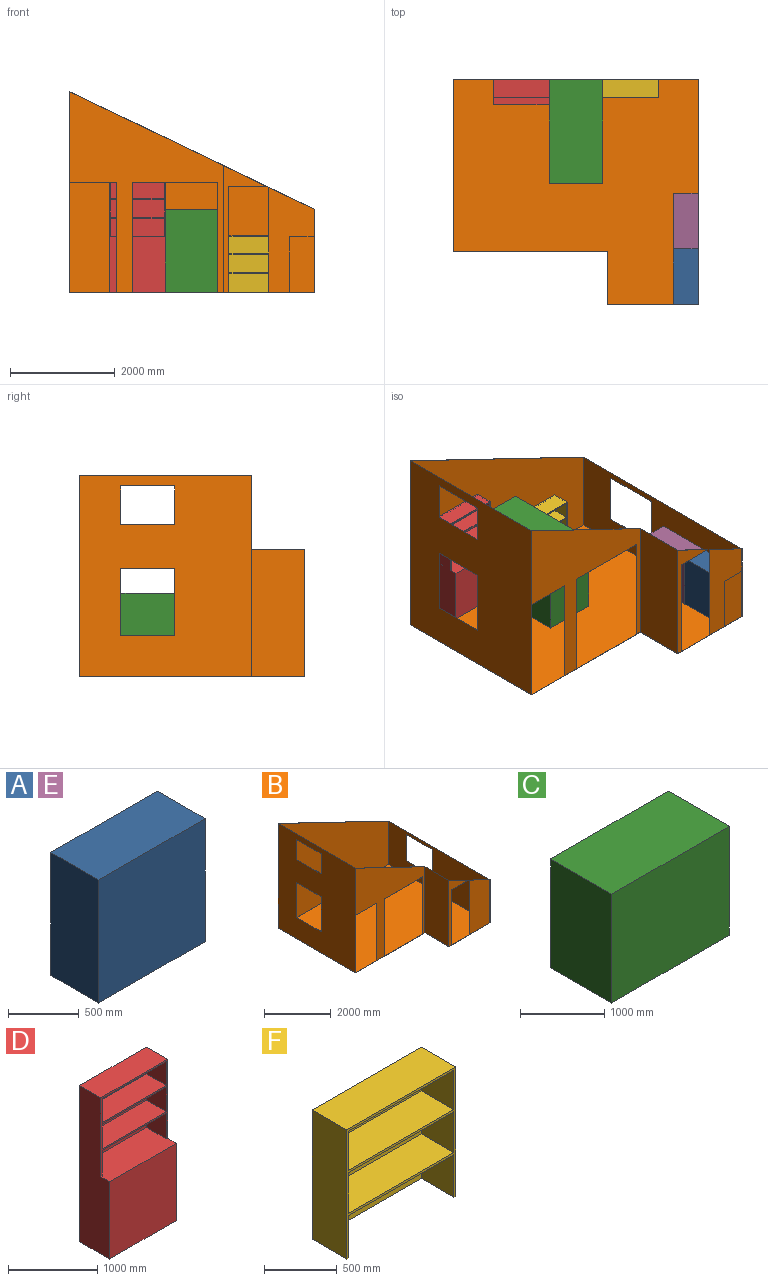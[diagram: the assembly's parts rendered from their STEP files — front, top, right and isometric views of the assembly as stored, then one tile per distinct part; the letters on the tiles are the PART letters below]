
ASSEMBLY  parts=6 mates=5
PART A: 6 faces, bbox 1060.5x476.3x1060.5 mm
  f0: plane 1060.45x1060.45mm, normal (0,1,0), area 1124554.2mm2, adj f2,f3,f4,f5
  f1: plane 1060.45x1060.45mm, normal (0,-1,0), area 1124554.2mm2, adj f2,f3,f4,f5
  f2: plane 1060.45x476.25mm, normal (1,0,0), area 505039.3mm2, adj f0,f1,f4,f5
  f3: plane 1060.45x476.25mm, normal (-1,0,0), area 505039.3mm2, adj f0,f1,f4,f5
  f4: plane 1060.45x476.25mm, normal (0,0,-1), area 505039.3mm2, adj f0,f1,f2,f3
  f5: plane 1060.45x476.25mm, normal (0,0,1), area 505039.3mm2, adj f0,f1,f2,f3
PART B: 37 faces, bbox 4680x4299x3842.5 mm
  f0: plane 2427.64x1741.49mm, normal (0,-1,0), area 1921155mm2, adj f3,f7,f9,f11,f15,f34,f35,f36
  f1: plane 2423.87x813.84mm, normal (0,1,0), area 346556.9mm2, adj f9,f13,f15,f35,f36
  f2: plane 3842.54x2938.46mm, normal (0,-1,0), area 3895113mm2, adj f3,f5,f9,f11,f15,f25,f26,f27
  f3: plane 4679.95x4298.95mm, normal (0,0,-1), area 17140440.5mm2, adj f0,f2,f5,f7,f10,f11,f24,f26
  f4: plane 3838.78x2938.46mm, normal (0,1,0), area 3891686.1mm2, adj f6,f9,f13,f15,f25,f26,f27,f28
  f5: plane 3842.54x3286.13mm, normal (-1,0,0), area 10525236.5mm2, adj f2,f3,f9,f10,f20,f21,f22,f23
  f6: plane 3838.78x3281.05mm, normal (1,0,0), area 10498724.5mm2, adj f4,f9,f12,f15,f20,f21,f22,f23
  f7: plane 4298.95x1589.09mm, normal (1,0,0), area 5769555mm2, adj f0,f3,f9,f10,f16,f17,f18,f19
  f8: plane 4293.87x1587.77mm, normal (-1,0,0), area 5755827.6mm2, adj f9,f12,f14,f15,f16,f17,f18,f19
  f9: plane 4679.95x4298.95mm, normal (0.43,0,0.9), area 50443.3mm2, adj f0,f1,f2,f4,f5,f6,f7,f8
  f10: plane 4679.95x3842.54mm, normal (0,1,0), area 12709881.3mm2, adj f3,f5,f7,f9
  f11: plane 2427.64x1012.83mm, normal (-1,0,0), area 2458770.6mm2, adj f0,f2,f3,f9
  f12: plane 4674.87x3838.78mm, normal (0,-1,0), area 12684210.8mm2, adj f6,f8,f9,f15
  f13: plane 2423.87x1012.83mm, normal (1,0,0), area 2454959.3mm2, adj f1,f4,f9,f15
  f14: plane 2005.82x868.2mm, normal (0,1,0), area 1559985.2mm2, adj f8,f9,f15,f34
  f15: plane 4674.87x4296.41mm, normal (0,0,1), area 17103236.2mm2, adj f0,f1,f2,f4,f6,f8,f12,f13
  f16: plane 1100.14x2.54mm, normal (0,0,-1), area 2794.3mm2, adj f7,f8,f17,f19
  f17: plane 965.2x2.54mm, normal (0,-1,0), area 2451.6mm2, adj f7,f8,f16,f18
  f18: plane 1100.14x2.54mm, normal (0,0,1), area 2794.3mm2, adj f7,f8,f17,f19
  f19: plane 965.2x2.54mm, normal (0,1,0), area 2451.6mm2, adj f7,f8,f16,f18
  f20: plane 1038.23x2.54mm, normal (0,0,-1), area 2637.1mm2, adj f5,f6,f21,f23
  f21: plane 1282.7x2.54mm, normal (0,-1,0), area 3258.1mm2, adj f5,f6,f20,f22
  f22: plane 1038.23x2.54mm, normal (0,0,1), area 2637.1mm2, adj f5,f6,f21,f23
  f23: plane 1282.7x2.54mm, normal (0,1,0), area 3258.1mm2, adj f5,f6,f20,f22
  f24: plane 2108.2x898.53mm, normal (0,-1,0), area 7630.6mm2, adj f3,f5,f6,f15,f25,f26
  f25: plane 898.53x2.54mm, normal (0,0,-1), area 2282.3mm2, adj f2,f4,f5,f24,f26
  f26: plane 2108.2x2.54mm, normal (-1,0,0), area 5354.8mm2, adj f2,f3,f4,f24,f25
  f27: plane 2105.66x2.54mm, normal (1,0,0), area 5348.4mm2, adj f2,f4,f15,f28
  f28: plane 1625.6x2.54mm, normal (0,0,-1), area 4129mm2, adj f2,f4,f27,f29
  f29: plane 2105.66x2.54mm, normal (-1,0,0), area 5348.4mm2, adj f2,f4,f15,f28
  f30: plane 1038.23x2.54mm, normal (0,0,1), area 2637.1mm2, adj f5,f6,f31,f32
  f31: plane 736.6x2.54mm, normal (0,1,0), area 1871mm2, adj f5,f6,f30,f33
  f32: plane 736.6x2.54mm, normal (0,-1,0), area 1871mm2, adj f5,f6,f30,f33
  f33: plane 1038.23x2.54mm, normal (0,0,-1), area 2637.1mm2, adj f5,f6,f31,f32
  f34: plane 2005.82x2.54mm, normal (-1,0,0), area 5094.8mm2, adj f0,f9,f14,f15
  f35: plane 721.76x2.54mm, normal (0,0,-1), area 1833.3mm2, adj f0,f1,f9,f36
  f36: plane 2032x2.54mm, normal (1,0,0), area 5161.3mm2, adj f0,f1,f15,f35
PART C: 6 faces, bbox 1981.2x1028.7x1585.8 mm
  f0: plane 1981.2x1585.85mm, normal (0,1,0), area 3141884mm2, adj f1,f3,f4,f5
  f1: plane 1585.85x1028.7mm, normal (-1,0,0), area 1631362.9mm2, adj f0,f2,f4,f5
  f2: plane 1981.2x1585.85mm, normal (0,-1,0), area 3141884mm2, adj f1,f3,f4,f5
  f3: plane 1585.85x1028.7mm, normal (1,0,0), area 1631362.9mm2, adj f0,f2,f4,f5
  f4: plane 1981.2x1028.7mm, normal (0,0,1), area 2038060.4mm2, adj f0,f1,f2,f3
  f5: plane 1981.2x1028.7mm, normal (0,0,-1), area 2038060.4mm2, adj f0,f1,f2,f3
PART D: 22 faces, bbox 1060.5x476.3x2146.3 mm
  f0: plane 330.2x317.5mm, normal (1,0,0), area 104838.5mm2, adj f6,f14,f17,f20
  f1: plane 330.2x317.5mm, normal (-1,0,0), area 104838.5mm2, adj f6,f14,f17,f20
  f2: plane 1022.35x342.9mm, normal (0,-1,0), area 350563.8mm2, adj f3,f4,f18,f21
  f3: plane 342.9x317.5mm, normal (1,0,0), area 108870.8mm2, adj f2,f6,f18,f21
  f4: plane 342.9x317.5mm, normal (-1,0,0), area 108870.8mm2, adj f2,f6,f18,f21
  f5: plane 1022.35x355.6mm, normal (0,-1,0), area 363547.7mm2, adj f13,f15,f16,f19
  f6: plane 1085.85x1060.45mm, normal (0,-1,0), area 99798.2mm2, adj f0,f1,f3,f4,f8,f9,f11,f13
  f7: plane 1060.45x1060.45mm, normal (0,-1,0), area 1124554.2mm2, adj f8,f11,f12,f13
  f8: plane 2146.3x476.25mm, normal (1,0,0), area 870482.1mm2, adj f6,f7,f9,f10,f12,f13
  f9: plane 1060.45x336.55mm, normal (0,0,1), area 356894.4mm2, adj f6,f8,f10,f11
  f10: plane 2146.3x1060.45mm, normal (0,1,0), area 2276043.8mm2, adj f8,f9,f11,f12
  f11: plane 2146.3x476.25mm, normal (-1,0,0), area 870482.1mm2, adj f6,f7,f9,f10,f12,f13
  f12: plane 1060.45x476.25mm, normal (0,0,-1), area 505039.3mm2, adj f7,f8,f10,f11
  f13: plane 1060.45x457.2mm, normal (0,0,1), area 472741mm2, adj f5,f6,f7,f8,f11,f15,f16
  f14: plane 1022.35x317.5mm, normal (0,0,-1), area 324596.1mm2, adj f0,f1,f6,f17
  f15: plane 355.6x317.5mm, normal (1,0,0), area 112903mm2, adj f5,f6,f13,f19
  f16: plane 355.6x317.5mm, normal (-1,0,0), area 112903mm2, adj f5,f6,f13,f19
  f17: plane 1022.35x330.2mm, normal (0,-1,0), area 337580mm2, adj f0,f1,f14,f20
  f18: plane 1022.35x317.5mm, normal (0,0,1), area 324596.1mm2, adj f2,f3,f4,f6
  f19: plane 1022.35x317.5mm, normal (0,0,-1), area 324596.1mm2, adj f5,f6,f15,f16
  f20: plane 1022.35x317.5mm, normal (0,0,1), area 324596.1mm2, adj f0,f1,f6,f17
  f21: plane 1022.35x317.5mm, normal (0,0,-1), area 324596.1mm2, adj f2,f3,f4,f6
PART E: same geometry as A
PART F: 20 faces, bbox 1060.5x336.6x1085.9 mm
  f0: plane 330.2x317.5mm, normal (1,0,0), area 104838.5mm2, adj f6,f11,f14,f17
  f1: plane 330.2x317.5mm, normal (-1,0,0), area 104838.5mm2, adj f6,f11,f14,f17
  f2: plane 1022.35x342.9mm, normal (0,-1,0), area 350563.8mm2, adj f3,f4,f15,f18
  f3: plane 342.9x317.5mm, normal (1,0,0), area 108870.8mm2, adj f2,f6,f15,f18
  f4: plane 342.9x317.5mm, normal (-1,0,0), area 108870.8mm2, adj f2,f6,f15,f18
  f5: plane 1022.35x355.6mm, normal (0,-1,0), area 363547.7mm2, adj f12,f13,f16,f19
  f6: plane 1085.85x1060.45mm, normal (0,-1,0), area 99798.2mm2, adj f0,f1,f3,f4,f7,f8,f10,f11
  f7: plane 1085.85x336.55mm, normal (1,0,0), area 365442.8mm2, adj f6,f8,f9,f19
  f8: plane 1060.45x336.55mm, normal (0,0,1), area 356894.4mm2, adj f6,f7,f9,f10
  f9: plane 1085.85x1060.45mm, normal (0,1,0), area 1151489.6mm2, adj f7,f8,f10,f19
  f10: plane 1085.85x336.55mm, normal (-1,0,0), area 365442.8mm2, adj f6,f8,f9,f19
  f11: plane 1022.35x317.5mm, normal (0,0,-1), area 324596.1mm2, adj f0,f1,f6,f14
  f12: plane 355.6x317.5mm, normal (1,0,0), area 112903mm2, adj f5,f6,f16,f19
  f13: plane 355.6x317.5mm, normal (-1,0,0), area 112903mm2, adj f5,f6,f16,f19
  f14: plane 1022.35x330.2mm, normal (0,-1,0), area 337580mm2, adj f0,f1,f11,f17
  f15: plane 1022.35x317.5mm, normal (0,0,1), area 324596.1mm2, adj f2,f3,f4,f6
  f16: plane 1022.35x317.5mm, normal (0,0,-1), area 324596.1mm2, adj f5,f6,f12,f13
  f17: plane 1022.35x317.5mm, normal (0,0,1), area 324596.1mm2, adj f0,f1,f6,f14
  f18: plane 1022.35x317.5mm, normal (0,0,-1), area 324596.1mm2, adj f2,f3,f4,f6
  f19: plane 1060.45x336.55mm, normal (0,0,-1), area 32298.3mm2, adj f5,f6,f7,f9,f10,f12,f13
PLACE A rot(axis=(0,0,-1),90deg) t=(3647.71,-3529.24,182.98)mm
PLACE B t=(-1029.7,-293.28,180.44)mm
PLACE C rot(axis=(0,0,-1),90deg) t=(1824.63,-295.82,182.98)mm
PLACE D t=(-264.52,-295.82,182.98)mm
PLACE E rot(axis=(0,0,-1),90deg) t=(3647.71,-2468.79,182.98)mm
PLACE F t=(1824.63,-295.82,-877.47)mm
MATE fastened D.f12 <-> C.f5  axis (0,0,-1) through (795.93,-295.82,182.98)mm
MATE fastened C.f1 <-> B.f12  axis (0,1,0) through (1310.28,-295.82,182.98)mm
MATE fastened A.f4 <-> B.f15  axis (0,0,-1) through (3647.71,-4589.69,182.98)mm
MATE fastened F.f19 <-> C.f5  axis (0,0,1) through (1824.63,-295.82,182.98)mm
MATE fastened E.f4 <-> A.f4  axis (0,0,-1) through (3647.71,-3529.24,182.98)mm
